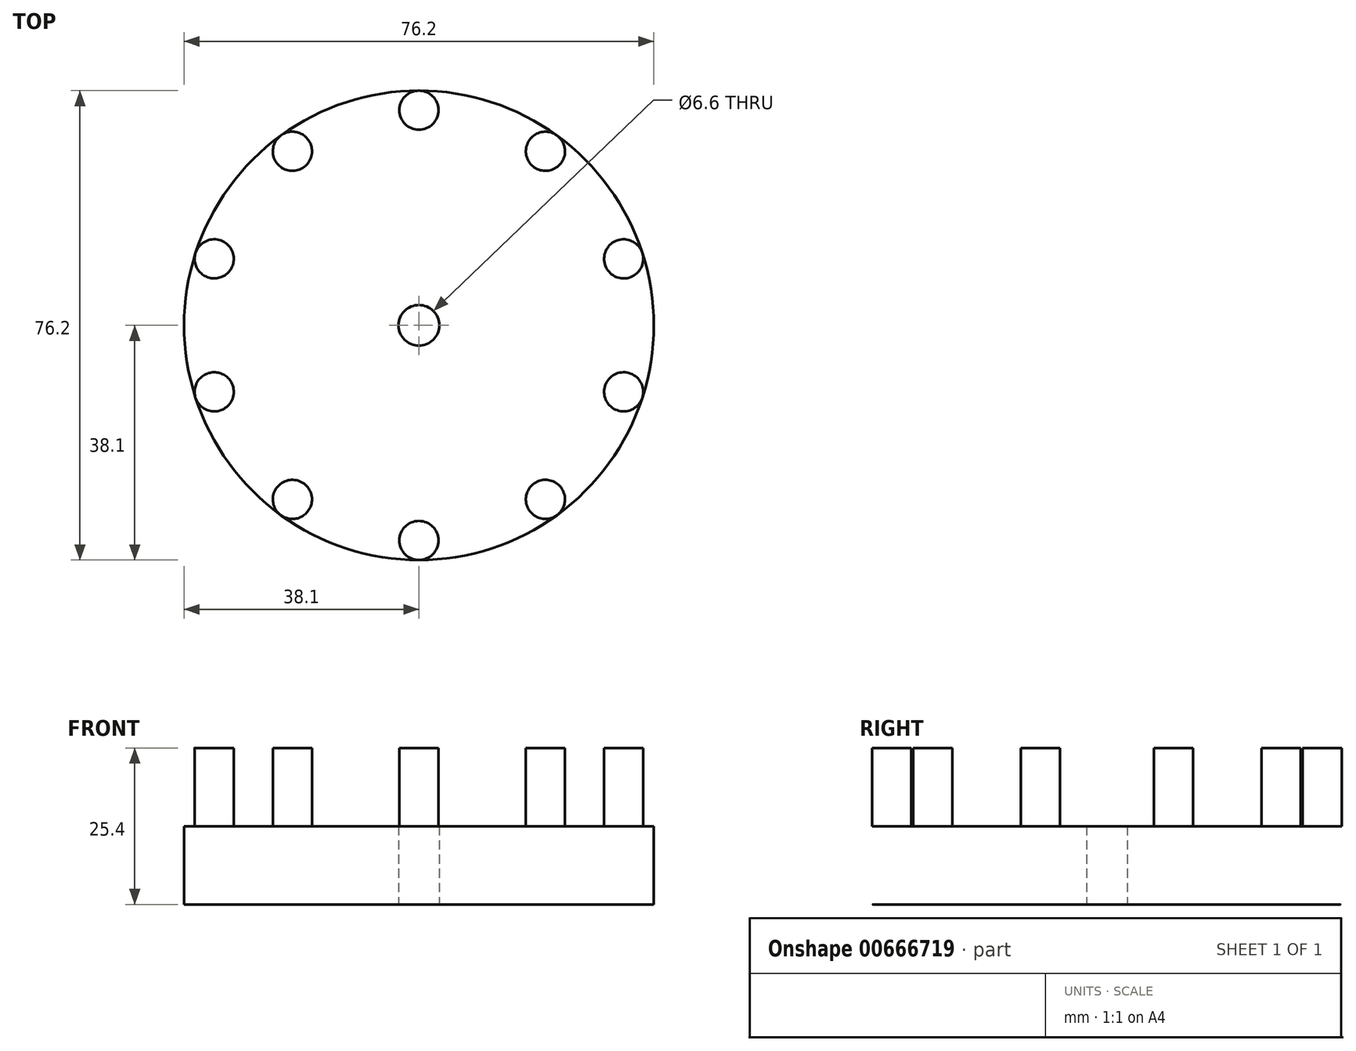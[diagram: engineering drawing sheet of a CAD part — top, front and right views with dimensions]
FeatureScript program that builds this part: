
annotation { "Feature Type Name" : "Feature", "Feature Type Description" : "" }
export const myFeature = defineFeature(function(context is Context, id is Id, definition is map)
    precondition{}
    {
        {
            var Q0;
            Q0=qCreatedBy(makeId("Top.planeOp"),FACE);
            var sketch = newSketch(context, id + "F0", { "sketchPlane" : qUnion([Q0])});
            skCircle(sketch, "E0", {"center": v(0, 0) * mm, "radius": 38.1 * mm});
            skCircle(sketch, "E1", {"center": v(0, 0) * mm, "radius": 3.3 * mm});
            skSolve(sketch);
        }
        {
            var Q0;
            Q0 = qSketchRegion(id + "F0", true);
            extrude(context, id + "F1", {"entities" : qUnion([Q0]), "depth" : 12.7 * mm, "offsetDistance" : 25.4 * mm});
        }
        {
            var Q0;
            Q0=makeQuery(id+"F1.opExtrude","CAP_FACE",FACE,{"disambiguationData":[OSD([sQuery(id+"F0.wireOp",EDGE,"E0")])],"isStart":false});
            var sketch = newSketch(context, id + "F2", { "sketchPlane" : qUnion([Q0])});
            skLineSegment(sketch, "E2", {"start": v(0, 38.1) * mm, "end": v(0, 34.93) * mm, "construction": true});
            skCircle(sketch, "E3", {"center": v(0, 34.93) * mm, "radius": 3.18 * mm});
            skCircle(sketch, "E4.1.0", {"center": v(-20.53, 28.25) * mm, "radius": 3.18 * mm});
            skCircle(sketch, "E4.2.0", {"center": v(-33.22, 10.8) * mm, "radius": 3.17 * mm});
            skCircle(sketch, "E4.3.0", {"center": v(-33.22, -10.8) * mm, "radius": 3.18 * mm});
            skCircle(sketch, "E4.4.0", {"center": v(-20.53, -28.25) * mm, "radius": 3.18 * mm});
            skCircle(sketch, "E4.5.0", {"center": v(0, -34.93) * mm, "radius": 3.18 * mm});
            skPoint(sketch, "E4.center", {"position": v(0, 0) * mm});
            skCircle(sketch, "E5.1.6.0", {"center": v(20.53, -28.25) * mm, "radius": 3.18 * mm});
            skCircle(sketch, "E5.1.7.0", {"center": v(33.22, -10.8) * mm, "radius": 3.18 * mm});
            skCircle(sketch, "E5.1.8.0", {"center": v(33.22, 10.8) * mm, "radius": 3.18 * mm});
            skCircle(sketch, "E5.1.9.0", {"center": v(20.53, 28.25) * mm, "radius": 3.18 * mm});
            skSolve(sketch);
        }
        {
            var Q0;
            Q0=makeQuery(id+"F2.imprint","IMPRINT",FACE,{"disambiguationData":[TD([[makeQuery(id+"F2.imprint","IMPRINT",EDGE,{"derivedFrom":sQuery(id+"F2.wireOp",EDGE,"E5.1.9.0")}),1.0]])]});
            var Q1;
            Q1=makeQuery(id+"F2.imprint","IMPRINT",FACE,{"disambiguationData":[TD([[makeQuery(id+"F2.imprint","IMPRINT",EDGE,{"derivedFrom":sQuery(id+"F2.wireOp",EDGE,"E5.1.8.0")}),1.0]])]});
            var Q2;
            Q2=makeQuery(id+"F2.imprint","IMPRINT",FACE,{"disambiguationData":[TD([[makeQuery(id+"F2.imprint","IMPRINT",EDGE,{"derivedFrom":sQuery(id+"F2.wireOp",EDGE,"E5.1.7.0")}),1.0]])]});
            var Q3;
            Q3=makeQuery(id+"F2.imprint","IMPRINT",FACE,{"disambiguationData":[TD([[makeQuery(id+"F2.imprint","IMPRINT",EDGE,{"derivedFrom":sQuery(id+"F2.wireOp",EDGE,"E5.1.6.0")}),1.0]])]});
            var Q4;
            Q4=sQuery(id+"F2.wireOp",EDGE,"E5.1.9.0");
            var Q5;
            Q5=sQuery(id+"F2.wireOp",EDGE,"E5.1.8.0");
            var Q6;
            Q6=sQuery(id+"F2.wireOp",EDGE,"E5.1.7.0");
            var Q7;
            Q7=sQuery(id+"F2.wireOp",EDGE,"E5.1.6.0");
            extrude(context, id + "F3", {"entities" : qUnion([Q0, Q1, Q2, Q3]), "operationType" : NewBodyOperationType.ADD, "surfaceEntities" : qUnion([Q4, Q5, Q6, Q7]), "depth" : 12.7 * mm, "offsetDistance" : 25.4 * mm});
        }
        {
            var Q0;
            Q0=makeQuery(id+"F2.imprint","IMPRINT",FACE,{"disambiguationData":[TD([[makeQuery(id+"F2.imprint","IMPRINT",EDGE,{"derivedFrom":sQuery(id+"F2.wireOp",EDGE,"E3")}),1.0]])]});
            var Q1;
            Q1=makeQuery(id+"F2.imprint","IMPRINT",FACE,{"disambiguationData":[TD([[makeQuery(id+"F2.imprint","IMPRINT",EDGE,{"derivedFrom":sQuery(id+"F2.wireOp",EDGE,"E4.1.0")}),1.0]])]});
            var Q2;
            Q2=makeQuery(id+"F2.imprint","IMPRINT",FACE,{"disambiguationData":[TD([[makeQuery(id+"F2.imprint","IMPRINT",EDGE,{"derivedFrom":sQuery(id+"F2.wireOp",EDGE,"E4.2.0")}),1.0]])]});
            var Q3;
            Q3=makeQuery(id+"F2.imprint","IMPRINT",FACE,{"disambiguationData":[TD([[makeQuery(id+"F2.imprint","IMPRINT",EDGE,{"derivedFrom":sQuery(id+"F2.wireOp",EDGE,"E4.3.0")}),1.0]])]});
            var Q4;
            Q4=makeQuery(id+"F2.imprint","IMPRINT",FACE,{"disambiguationData":[TD([[makeQuery(id+"F2.imprint","IMPRINT",EDGE,{"derivedFrom":sQuery(id+"F2.wireOp",EDGE,"E4.4.0")}),1.0]])]});
            var Q5;
            Q5=makeQuery(id+"F2.imprint","IMPRINT",FACE,{"disambiguationData":[TD([[makeQuery(id+"F2.imprint","IMPRINT",EDGE,{"derivedFrom":sQuery(id+"F2.wireOp",EDGE,"E4.5.0")}),1.0]])]});
            var Q6;
            Q6=sQuery(id+"F2.wireOp",EDGE,"E3");
            var Q7;
            Q7=sQuery(id+"F2.wireOp",EDGE,"E4.1.0");
            extrude(context, id + "F4", {"entities" : qUnion([Q0, Q1, Q2, Q3, Q4, Q5]), "operationType" : NewBodyOperationType.ADD, "surfaceEntities" : qUnion([Q6, Q7]), "depth" : 12.7 * mm, "offsetDistance" : 25.4 * mm});
        }
    });
